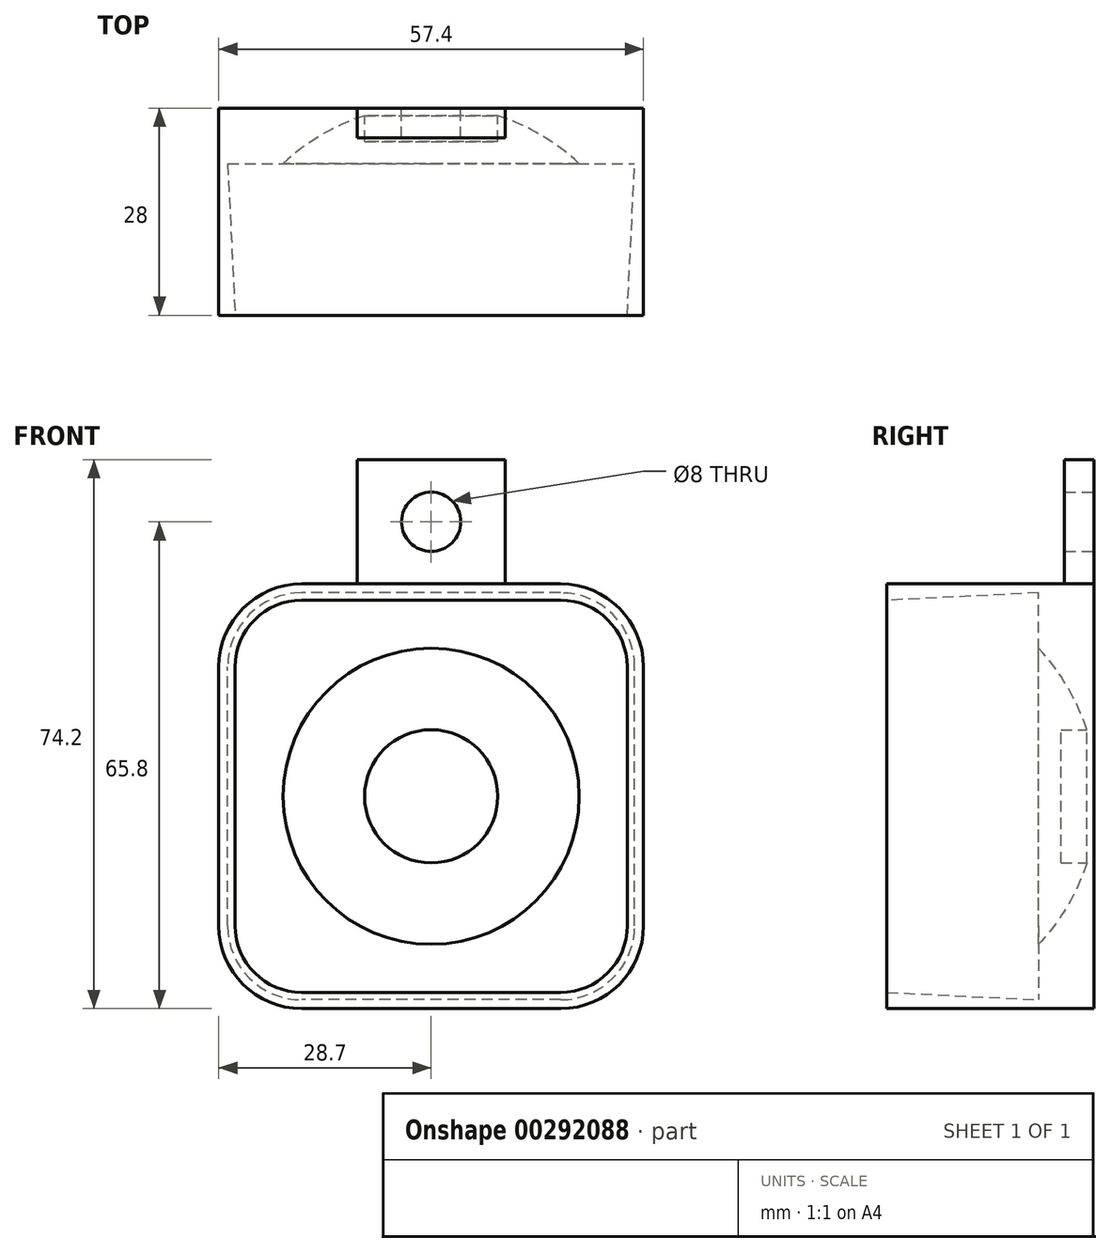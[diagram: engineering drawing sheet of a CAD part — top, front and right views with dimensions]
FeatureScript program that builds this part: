
annotation { "Feature Type Name" : "Feature", "Feature Type Description" : "" }
export const myFeature = defineFeature(function(context is Context, id is Id, definition is map)
    precondition{}
    {
        {
            var Q0;
            Q0=qCreatedBy(makeId("Front.planeOp"),FACE);
            var sketch = newSketch(context, id + "F0", { "sketchPlane" : qUnion([Q0])});
            skLineSegment(sketch, "E0.bottom", {"start": v(17.5, -27.5) * mm, "end": v(-17.5, -27.5) * mm});
            skLineSegment(sketch, "E0.top", {"start": v(17.5, 27.5) * mm, "end": v(-17.5, 27.5) * mm});
            skLineSegment(sketch, "E0.left", {"start": v(27.5, -17.5) * mm, "end": v(27.5, 17.5) * mm});
            skLineSegment(sketch, "E0.right", {"start": v(-27.5, -17.5) * mm, "end": v(-27.5, 17.5) * mm});
            skPoint(sketch, "E0.middle", {"position": v(0, 0) * mm});
            skPoint(sketch, "E1.visualSharp", {"position": v(27.5, -27.5) * mm});
            skArc(sketch, "E1.filletArc", {"start": v(17.5, -27.5) * mm, "mid": v(24.57, -24.57) * mm, "end": v(27.5, -17.5) * mm});
            skPoint(sketch, "E2.visualSharp", {"position": v(-27.5, -27.5) * mm});
            skArc(sketch, "E2.filletArc", {"start": v(-27.5, -17.5) * mm, "mid": v(-24.57, -24.57) * mm, "end": v(-17.5, -27.5) * mm});
            skPoint(sketch, "E3.visualSharp", {"position": v(-27.5, 27.5) * mm});
            skArc(sketch, "E3.filletArc", {"start": v(-17.5, 27.5) * mm, "mid": v(-24.57, 24.57) * mm, "end": v(-27.5, 17.5) * mm});
            skPoint(sketch, "E4.visualSharp", {"position": v(27.5, 27.5) * mm});
            skArc(sketch, "E4.filletArc", {"start": v(27.5, 17.5) * mm, "mid": v(24.57, 24.57) * mm, "end": v(17.5, 27.5) * mm});
            skCircle(sketch, "E5", {"center": v(0, 0) * mm, "radius": 20 * mm});
            skCircle(sketch, "E6", {"center": v(0, 0) * mm, "radius": 9 * mm});
            skArc(sketch, "E7.0", {"start": v(25.5, 17.5) * mm, "mid": v(23.16, 23.16) * mm, "end": v(17.5, 25.5) * mm});
            skLineSegment(sketch, "E7.1", {"start": v(25.5, -17.5) * mm, "end": v(25.5, 17.5) * mm});
            skLineSegment(sketch, "E7.2", {"start": v(17.5, 25.5) * mm, "end": v(-17.5, 25.5) * mm});
            skArc(sketch, "E7.3", {"start": v(17.5, -25.5) * mm, "mid": v(23.16, -23.16) * mm, "end": v(25.5, -17.5) * mm});
            skArc(sketch, "E7.4", {"start": v(-17.5, 25.5) * mm, "mid": v(-23.16, 23.16) * mm, "end": v(-25.5, 17.5) * mm});
            skLineSegment(sketch, "E7.5", {"start": v(-25.5, -17.5) * mm, "end": v(-25.5, 17.5) * mm});
            skArc(sketch, "E7.6", {"start": v(-25.5, -17.5) * mm, "mid": v(-23.16, -23.16) * mm, "end": v(-17.5, -25.5) * mm});
            skLineSegment(sketch, "E7.7", {"start": v(17.5, -25.5) * mm, "end": v(-17.5, -25.5) * mm});
            skArc(sketch, "E8.0", {"start": v(26.5, 17.5) * mm, "mid": v(23.86, 23.86) * mm, "end": v(17.5, 26.5) * mm});
            skLineSegment(sketch, "E8.1", {"start": v(26.5, -17.5) * mm, "end": v(26.5, 17.5) * mm});
            skLineSegment(sketch, "E8.2", {"start": v(17.5, 26.5) * mm, "end": v(-17.5, 26.5) * mm});
            skArc(sketch, "E8.3", {"start": v(17.5, -26.5) * mm, "mid": v(23.86, -23.86) * mm, "end": v(26.5, -17.5) * mm});
            skArc(sketch, "E8.4", {"start": v(-17.5, 26.5) * mm, "mid": v(-23.86, 23.86) * mm, "end": v(-26.5, 17.5) * mm});
            skLineSegment(sketch, "E8.5", {"start": v(-26.5, -17.5) * mm, "end": v(-26.5, 17.5) * mm});
            skArc(sketch, "E8.6", {"start": v(-26.5, -17.5) * mm, "mid": v(-23.86, -23.86) * mm, "end": v(-17.5, -26.5) * mm});
            skLineSegment(sketch, "E8.7", {"start": v(17.5, -26.5) * mm, "end": v(-17.5, -26.5) * mm});
            skSolve(sketch);
        }
        {
            var Q0;
            Q0=qCreatedBy(makeId("Top.planeOp"),FACE);
            var sketch = newSketch(context, id + "F1", { "sketchPlane" : qUnion([Q0])});
            skLineSegment(sketch, "E9.0", {"start": v(20, 0) * mm, "end": v(-20, 0) * mm});
            skLineSegment(sketch, "E9.1", {"start": v(9, 0) * mm, "end": v(-9, 0) * mm});
            skLineSegment(sketch, "E10", {"start": v(0, 0) * mm, "end": v(0, 6.5) * mm});
            skLineSegment(sketch, "E11", {"start": v(-20, 6.5) * mm, "end": v(20, 6.5) * mm});
            skLineSegment(sketch, "E12", {"start": v(9, 6.5) * mm, "end": v(9, 0) * mm, "construction": true});
            skLineSegment(sketch, "E13", {"start": v(-20, 0) * mm, "end": v(-20, 6.5) * mm, "construction": true});
            skLineSegment(sketch, "E14", {"start": v(20, 0) * mm, "end": v(20, 6.5) * mm, "construction": true});
            skLineSegment(sketch, "E15", {"start": v(-9, 0) * mm, "end": v(-9, 6.5) * mm, "construction": true});
            skArc(sketch, "E16", {"start": v(20, 0) * mm, "mid": v(0, 7.92) * mm, "end": v(-20, 0) * mm});
            skSolve(sketch);
        }
        {
            var Q0;
            Q0=makeQuery(id+"F0.imprint","IMPRINT",FACE,{"disambiguationData":[TD([[makeQuery(id+"F0.imprint","IMPRINT",EDGE,{"derivedFrom":sQuery(id+"F0.wireOp",EDGE,"E5")}),-1.0]])]});
            var Q1;
            Q1=makeQuery(id+"F0.imprint","IMPRINT",FACE,{"disambiguationData":[TD([[makeQuery(id+"F0.imprint","IMPRINT",EDGE,{"derivedFrom":sQuery(id+"F0.wireOp",EDGE,"E7.0")}),-1.0]])]});
            var Q2;
            Q2=makeQuery(id+"F0.imprint","IMPRINT",FACE,{"disambiguationData":[TD([[makeQuery(id+"F0.imprint","IMPRINT",EDGE,{"derivedFrom":sQuery(id+"F0.wireOp",EDGE,"E5")}),1.0]])]});
            var Q3;
            Q3=makeQuery(id+"F0.imprint","IMPRINT",FACE,{"disambiguationData":[TD([[makeQuery(id+"F0.imprint","IMPRINT",EDGE,{"derivedFrom":sQuery(id+"F0.wireOp",EDGE,"E6")}),1.0]])]});
            var Q4;
            Q4=makeQuery(id+"F0.imprint","IMPRINT",FACE,{"disambiguationData":[TD([[makeQuery(id+"F0.imprint","IMPRINT",EDGE,{"derivedFrom":sQuery(id+"F0.wireOp",EDGE,"E0.bottom")}),-1.0]])]});
            extrude(context, id + "F2", {"entities" : qUnion([Q0, Q1, Q2, Q3, Q4]), "depth" : 20.5 * mm});
        }
        {
            var Q0;
            Q0=makeQuery(id+"F2.opExtrude","CAP_FACE",FACE,{"disambiguationData":[OSD([sQuery(id+"F0.wireOp",EDGE,"E8.0"),sQuery(id+"F0.wireOp",EDGE,"E8.1"),sQuery(id+"F0.wireOp",EDGE,"E8.2"),sQuery(id+"F0.wireOp",EDGE,"E8.3"),sQuery(id+"F0.wireOp",EDGE,"E8.4"),sQuery(id+"F0.wireOp",EDGE,"E8.5"),sQuery(id+"F0.wireOp",EDGE,"E8.6"),sQuery(id+"F0.wireOp",EDGE,"E8.7")])],"isStart":false});
            var Q1;
            Q1=makeQuery(id+"F2.opExtrude","CAP_FACE",FACE,{"disambiguationData":[OSD([sQuery(id+"F0.wireOp",EDGE,"E0.bottom"),sQuery(id+"F0.wireOp",EDGE,"E0.top"),sQuery(id+"F0.wireOp",EDGE,"E0.left"),sQuery(id+"F0.wireOp",EDGE,"E0.right"),sQuery(id+"F0.wireOp",EDGE,"E1.filletArc"),sQuery(id+"F0.wireOp",EDGE,"E2.filletArc"),sQuery(id+"F0.wireOp",EDGE,"E3.filletArc"),sQuery(id+"F0.wireOp",EDGE,"E4.filletArc")])],"isStart":false});
            chamfer(context, id + "F3", {"entities" : qUnion([Q0, Q1]), "chamferType" : ChamferType.TWO_OFFSETS, "width1" : 1 * mm, "oppositeDirection" : true, "width2" : 20.5 * mm, "tangentPropagation" : true});
        }
        {
            var Q0;
            {var subQ1=sQuery(id+"F1.wireOp",EDGE,"E10");Q0=makeQuery(id+"F1.imprint","IMPRINT",FACE,{"disambiguationData":[TD([[makeQuery(id+"F1.imprint","IMPRINT",EDGE,{"derivedFrom":subQ1}),-1.0]])]});}
            var Q1;
            Q1=sQuery(id+"F1.wireOp",EDGE,"E10");
            revolve(context, id + "F4", {"operationType" : NewBodyOperationType.ADD, "entities" : qUnion([Q0]), "axis" : qUnion([Q1]), "revolveType" : RevolveType.FULL});
        }
        {
            var Q0;
            Q0=makeQuery(id+"F4.opRevolve","SWEPT_FACE",FACE,{"disambiguationData":[OSD([sQuery(id+"F1.wireOp",EDGE,"E11")])]});
            extrude(context, id + "F5", {"entities" : qUnion([Q0]), "operationType" : NewBodyOperationType.REMOVE, "oppositeDirection" : true, "depth" : 3.5 * mm});
        }
        {
            var Q0;
            Q0=makeQuery(id+"F2.opExtrude","CAP_FACE",FACE,{"disambiguationData":[OSD([sQuery(id+"F0.wireOp",EDGE,"E0.bottom"),sQuery(id+"F0.wireOp",EDGE,"E0.top"),sQuery(id+"F0.wireOp",EDGE,"E0.left"),sQuery(id+"F0.wireOp",EDGE,"E0.right"),sQuery(id+"F0.wireOp",EDGE,"E1.filletArc"),sQuery(id+"F0.wireOp",EDGE,"E2.filletArc"),sQuery(id+"F0.wireOp",EDGE,"E3.filletArc"),sQuery(id+"F0.wireOp",EDGE,"E4.filletArc")])],"isStart":false});
            var sketch = newSketch(context, id + "F6", { "sketchPlane" : qUnion([Q0])});
            skLineSegment(sketch, "E17.1", {"start": v(-27.5, -17.5) * mm, "end": v(-27.5, 17.5) * mm, "construction": true});
            skArc(sketch, "E17.2", {"start": v(-17.5, 27.5) * mm, "mid": v(-24.57, 24.57) * mm, "end": v(-27.5, 17.5) * mm, "construction": true});
            skLineSegment(sketch, "E17.3", {"start": v(17.5, 27.5) * mm, "end": v(-17.5, 27.5) * mm, "construction": true});
            skArc(sketch, "E17.4", {"start": v(27.5, 17.5) * mm, "mid": v(24.57, 24.57) * mm, "end": v(17.5, 27.5) * mm, "construction": true});
            skLineSegment(sketch, "E17.5", {"start": v(27.5, -17.5) * mm, "end": v(27.5, 17.5) * mm, "construction": true});
            skArc(sketch, "E17.6", {"start": v(17.5, -27.5) * mm, "mid": v(24.57, -24.57) * mm, "end": v(27.5, -17.5) * mm, "construction": true});
            skLineSegment(sketch, "E17.7", {"start": v(17.5, -27.5) * mm, "end": v(-17.5, -27.5) * mm, "construction": true});
            skArc(sketch, "E17.8", {"start": v(-27.5, -17.5) * mm, "mid": v(-24.57, -24.57) * mm, "end": v(-17.5, -27.5) * mm, "construction": true});
            skArc(sketch, "E18.0", {"start": v(-28.7, -17.5) * mm, "mid": v(-25.42, -25.42) * mm, "end": v(-17.5, -28.7) * mm});
            skLineSegment(sketch, "E18.1", {"start": v(17.5, -28.7) * mm, "end": v(-17.5, -28.7) * mm});
            skLineSegment(sketch, "E18.2", {"start": v(-28.7, -17.5) * mm, "end": v(-28.7, 17.5) * mm});
            skArc(sketch, "E18.3", {"start": v(17.5, -28.7) * mm, "mid": v(25.42, -25.42) * mm, "end": v(28.7, -17.5) * mm});
            skArc(sketch, "E18.4", {"start": v(-17.5, 28.7) * mm, "mid": v(-25.42, 25.42) * mm, "end": v(-28.7, 17.5) * mm});
            skLineSegment(sketch, "E18.5", {"start": v(17.5, 28.7) * mm, "end": v(-17.5, 28.7) * mm});
            skArc(sketch, "E18.6", {"start": v(28.7, 17.5) * mm, "mid": v(25.42, 25.42) * mm, "end": v(17.5, 28.7) * mm});
            skLineSegment(sketch, "E18.7", {"start": v(28.7, -17.5) * mm, "end": v(28.7, 17.5) * mm});
            skSolve(sketch);
        }
        {
            var Q0;
            Q0=makeQuery(id+"F6.imprint","IMPRINT",FACE,{"disambiguationData":[TD([[makeQuery(id+"F6.imprint","IMPRINT",EDGE,{"derivedFrom":sQuery(id+"F6.wireOp",EDGE,"af4fa2f0-2a9d-4e13-bc83-dd4879622614.0")}),1.0]])]});
            var Q1;
            {var subQ0=sQuery(id+"F0.wireOp",EDGE,"E4.filletArc");var subQ1=sQuery(id+"F0.wireOp",EDGE,"E3.filletArc");var subQ2=sQuery(id+"F0.wireOp",EDGE,"E2.filletArc");var subQ3=sQuery(id+"F0.wireOp",EDGE,"E1.filletArc");var subQ4=sQuery(id+"F0.wireOp",EDGE,"E0.right");var subQ5=sQuery(id+"F0.wireOp",EDGE,"E0.left");var subQ6=sQuery(id+"F0.wireOp",EDGE,"E0.top");var subQ7=sQuery(id+"F0.wireOp",EDGE,"E0.bottom");var subQ8=makeQuery(id+"F2.opExtrude","CAP_FACE",FACE,{"disambiguationData":[OSD([subQ7,subQ6,subQ5,subQ4,subQ3,subQ2,subQ1,subQ0])],"isStart":false});Q1=makeQuery(id+"F6.imprint","IMPRINT",FACE,{"disambiguationData":[TD([[makeQuery(id+"F6.imprint","IMPRINT",EDGE,{"derivedFrom":makeQuery(id+"F3.opChamfer","BLEND_EDGE",EDGE,{"blendedFrom":[makeQuery(id+"F2.opExtrude","CAP_EDGE",EDGE,{"disambiguationData":[OSD([subQ7])],"isStart":false}),subQ8],"blendedInto":[subQ8]})}),1.0]])]});}
            var Q2;
            Q2=makeQuery(id+"F6.imprint","IMPRINT",FACE,{"disambiguationData":[TD([[makeQuery(id+"F6.imprint","IMPRINT",EDGE,{"derivedFrom":sQuery(id+"F6.wireOp",EDGE,"E18.0")}),1.0]])]});
            extrude(context, id + "F7", {"entities" : qUnion([Q0, Q1, Q2]), "oppositeDirection" : true, "depth" : 28 * mm});
        }
        {
            var Q0;
            Q0=makeQuery(id+"F2.opExtrude","SWEPT_BODY",BODY,{"disambiguationData":[OSD([sQuery(id+"F0.wireOp",EDGE,"E0.bottom"),sQuery(id+"F0.wireOp",EDGE,"E0.top"),sQuery(id+"F0.wireOp",EDGE,"E0.left"),sQuery(id+"F0.wireOp",EDGE,"E0.right"),sQuery(id+"F0.wireOp",EDGE,"E1.filletArc"),sQuery(id+"F0.wireOp",EDGE,"E2.filletArc"),sQuery(id+"F0.wireOp",EDGE,"E3.filletArc"),sQuery(id+"F0.wireOp",EDGE,"E4.filletArc")])]});
            var Q1;
            Q1=makeQuery(id+"F7.opExtrude","SWEPT_BODY",BODY,{"disambiguationData":[OSD([sQuery(id+"F6.wireOp",EDGE,"E18.0"),sQuery(id+"F6.wireOp",EDGE,"E18.1"),sQuery(id+"F6.wireOp",EDGE,"E18.2"),sQuery(id+"F6.wireOp",EDGE,"E18.3"),sQuery(id+"F6.wireOp",EDGE,"E18.4"),sQuery(id+"F6.wireOp",EDGE,"E18.5"),sQuery(id+"F6.wireOp",EDGE,"E18.6"),sQuery(id+"F6.wireOp",EDGE,"E18.7")])]});
            booleanBodies(context, id + "F8", {"operationType" : BooleanOperationType.SUBTRACTION, "tools" : qUnion([Q0]), "targets" : qUnion([Q1])});
        }
        {
            var Q0;
            Q0=makeQuery(id+"F7.opExtrude","CAP_FACE",FACE,{"disambiguationData":[OSD([sQuery(id+"F6.wireOp",EDGE,"E18.0"),sQuery(id+"F6.wireOp",EDGE,"E18.1"),sQuery(id+"F6.wireOp",EDGE,"E18.2"),sQuery(id+"F6.wireOp",EDGE,"E18.3"),sQuery(id+"F6.wireOp",EDGE,"E18.4"),sQuery(id+"F6.wireOp",EDGE,"E18.5"),sQuery(id+"F6.wireOp",EDGE,"E18.6"),sQuery(id+"F6.wireOp",EDGE,"E18.7")])],"isStart":false});
            var sketch = newSketch(context, id + "F9", { "sketchPlane" : qUnion([Q0])});
            skLineSegment(sketch, "E19", {"start": v(-10, 20.5) * mm, "end": v(-10, 45.5) * mm});
            skLineSegment(sketch, "E20", {"start": v(-10, 45.5) * mm, "end": v(10, 45.5) * mm});
            skLineSegment(sketch, "E21", {"start": v(10, 45.5) * mm, "end": v(10, 20.5) * mm});
            skLineSegment(sketch, "E22", {"start": v(10, 20.5) * mm, "end": v(-10, 20.5) * mm});
            skLineSegment(sketch, "E23", {"start": v(-20.5, 20.5) * mm, "end": v(20.5, 20.5) * mm, "construction": true});
            skPoint(sketch, "E24", {"position": v(0, 20.5) * mm});
            skLineSegment(sketch, "E25", {"start": v(0, 20.5) * mm, "end": v(0, 45.5) * mm, "construction": true});
            skCircle(sketch, "E26", {"center": v(0, 37.1) * mm, "radius": 4 * mm});
            skLineSegment(sketch, "E27", {"start": v(-5.22, 28.7) * mm, "end": v(-5.22, 45.5) * mm, "construction": true});
            skPoint(sketch, "E28", {"position": v(-5.22, 37.1) * mm});
            skLineSegment(sketch, "E29.0", {"start": v(-17.5, 28.7) * mm, "end": v(17.5, 28.7) * mm});
            skArc(sketch, "E29.1", {"start": v(-28.7, 17.5) * mm, "mid": v(-25.42, 25.42) * mm, "end": v(-17.5, 28.7) * mm});
            skLineSegment(sketch, "E29.2", {"start": v(-28.7, -17.5) * mm, "end": v(-28.7, 17.5) * mm});
            skArc(sketch, "E29.3", {"start": v(-17.5, -28.7) * mm, "mid": v(-25.42, -25.42) * mm, "end": v(-28.7, -17.5) * mm});
            skLineSegment(sketch, "E29.4", {"start": v(-17.5, -28.7) * mm, "end": v(17.5, -28.7) * mm});
            skArc(sketch, "E29.5", {"start": v(28.7, -17.5) * mm, "mid": v(25.42, -25.42) * mm, "end": v(17.5, -28.7) * mm});
            skLineSegment(sketch, "E29.6", {"start": v(28.7, -17.5) * mm, "end": v(28.7, 17.5) * mm});
            skArc(sketch, "E29.7", {"start": v(17.5, 28.7) * mm, "mid": v(25.42, 25.42) * mm, "end": v(28.7, 17.5) * mm});
            skSolve(sketch);
        }
        {
            var Q0;
            {var subQ5=sQuery(id+"F9.wireOp",EDGE,"E22");Q0=makeQuery(id+"F9.imprint","IMPRINT",FACE,{"disambiguationData":[TD([[makeQuery(id+"F9.imprint","IMPRINT",EDGE,{"derivedFrom":subQ5}),-1.0]])]});}
            var Q1;
            {var subQ1=sQuery(id+"F9.wireOp",EDGE,"E20");Q1=makeQuery(id+"F9.imprint","IMPRINT",FACE,{"disambiguationData":[TD([[makeQuery(id+"F9.imprint","IMPRINT",EDGE,{"derivedFrom":subQ1}),-1.0]])]});}
            extrude(context, id + "F10", {"entities" : qUnion([Q0, Q1]), "operationType" : NewBodyOperationType.ADD, "oppositeDirection" : true, "depth" : 4 * mm});
        }
    });
